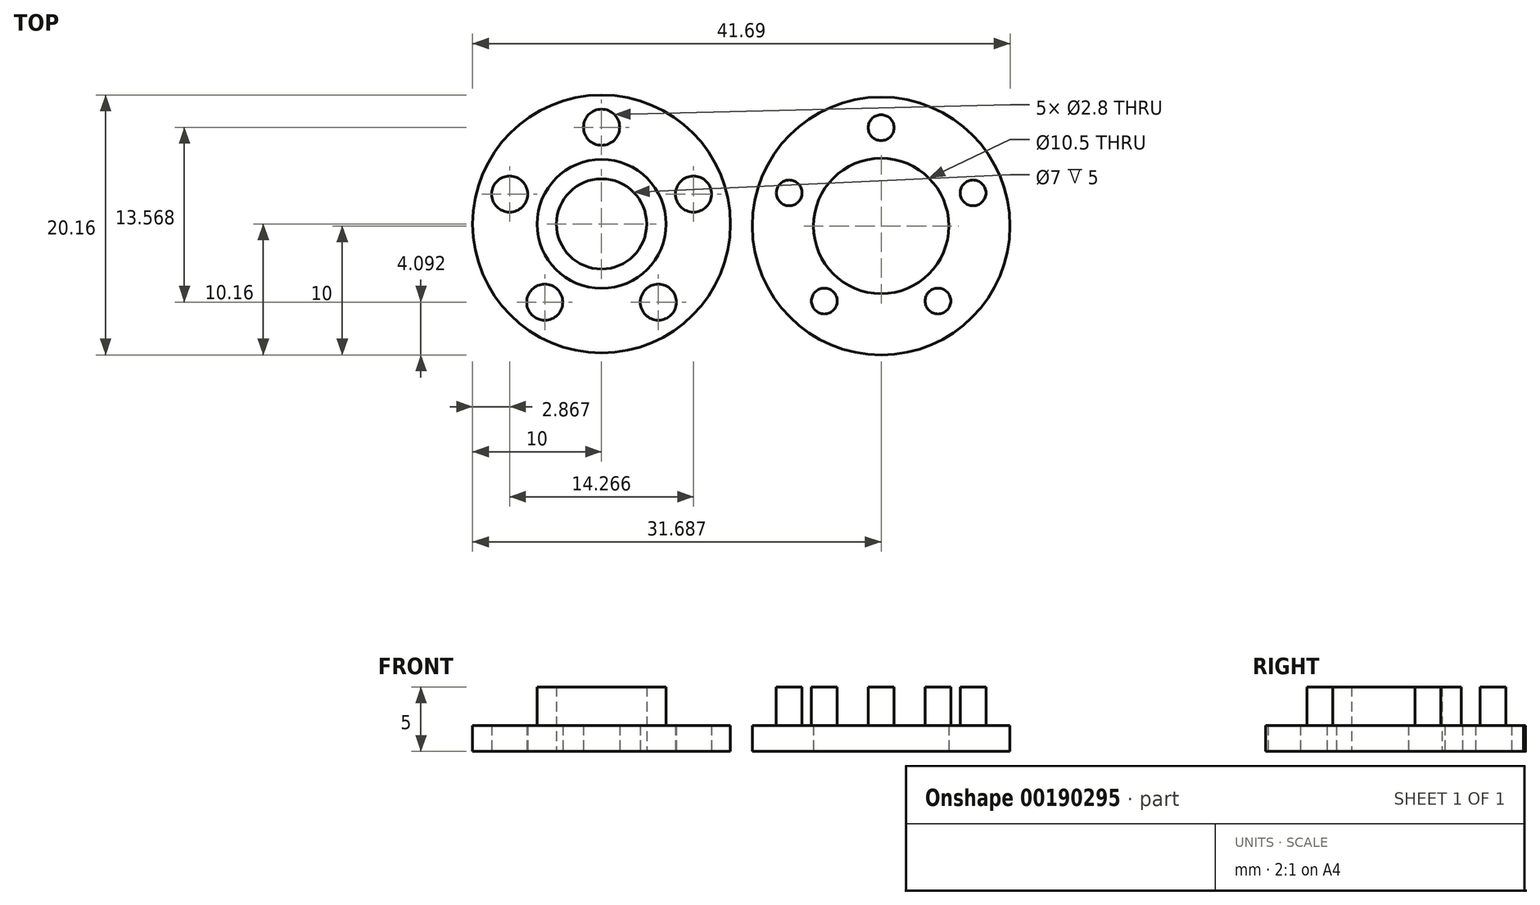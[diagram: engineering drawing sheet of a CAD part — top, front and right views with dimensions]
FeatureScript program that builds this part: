
annotation { "Feature Type Name" : "Feature", "Feature Type Description" : "" }
export const myFeature = defineFeature(function(context is Context, id is Id, definition is map)
    precondition{}
    {
        {
            var Q0;
            Q0=qCreatedBy(makeId("Top.planeOp"),FACE);
            var sketch = newSketch(context, id + "F0", { "sketchPlane" : qUnion([Q0])});
            skCircle(sketch, "E0", {"center": v(0, 0) * mm, "radius": 10 * mm});
            skCircle(sketch, "E1", {"center": v(0, 0) * mm, "radius": 5 * mm});
            skCircle(sketch, "E2", {"center": v(0, 7.5) * mm, "radius": 1.4 * mm});
            skLineSegment(sketch, "E3", {"start": v(0, 10) * mm, "end": v(0, 7.5) * mm, "construction": true});
            skLineSegment(sketch, "E4", {"start": v(0, 5) * mm, "end": v(0, 7.5) * mm, "construction": true});
            skCircle(sketch, "E5.1.0", {"center": v(-7.13, 2.32) * mm, "radius": 1.4 * mm});
            skCircle(sketch, "E5.2.0", {"center": v(-4.4, -6.07) * mm, "radius": 1.4 * mm});
            skCircle(sketch, "E5.3.0", {"center": v(4.4, -6.07) * mm, "radius": 1.4 * mm});
            skCircle(sketch, "E5.4.0", {"center": v(7.13, 2.32) * mm, "radius": 1.4 * mm});
            skSolve(sketch);
        }
        {
            var Q0;
            Q0=makeQuery(id+"F0.imprint","IMPRINT",FACE,{"disambiguationData":[TD([[makeQuery(id+"F0.imprint","IMPRINT",EDGE,{"derivedFrom":sQuery(id+"F0.wireOp",EDGE,"E0")}),1.0]])]});
            extrude(context, id + "F1", {"entities" : qUnion([Q0]), "depth" : 2 * mm});
        }
        {
            var Q0;
            Q0=qCreatedBy(makeId("Top.planeOp"),FACE);
            var sketch = newSketch(context, id + "F2", { "sketchPlane" : qUnion([Q0])});
            skCircle(sketch, "E6", {"center": v(21.69, -0.16) * mm, "radius": 10 * mm});
            skCircle(sketch, "E7", {"center": v(21.69, -0.16) * mm, "radius": 5.25 * mm});
            skCircle(sketch, "E8", {"center": v(21.69, 7.46) * mm, "radius": 1 * mm});
            skLineSegment(sketch, "E9", {"start": v(21.69, 9.84) * mm, "end": v(21.69, 7.46) * mm, "construction": true});
            skLineSegment(sketch, "E10", {"start": v(21.69, 5.09) * mm, "end": v(21.69, 7.46) * mm, "construction": true});
            skCircle(sketch, "E11.1.0", {"center": v(14.55, 2.4) * mm, "radius": 1 * mm});
            skCircle(sketch, "E11.2.0", {"center": v(17.28, -5.98) * mm, "radius": 1 * mm});
            skCircle(sketch, "E11.3.0", {"center": v(26.1, -5.98) * mm, "radius": 1 * mm});
            skCircle(sketch, "E11.4.0", {"center": v(28.82, 2.4) * mm, "radius": 1 * mm});
            skLineSegment(sketch, "E12", {"start": v(12.74, -4.62) * mm, "end": v(21.69, -0.16) * mm, "construction": true});
            skLineSegment(sketch, "E13", {"start": v(21.69, -0.16) * mm, "end": v(30.64, 4.3) * mm, "construction": true});
            skSolve(sketch);
        }
        {
            var Q0;
            Q0=qCreatedBy(makeId("Top.planeOp"),FACE);
            var sketch = newSketch(context, id + "F3", { "sketchPlane" : qUnion([Q0])});
            skCircle(sketch, "E14", {"center": v(0, 0) * mm, "radius": 3.5 * mm});
            skCircle(sketch, "E15", {"center": v(0, 0) * mm, "radius": 5 * mm});
            skSolve(sketch);
        }
        {
            var Q0;
            Q0=makeQuery(id+"F3.imprint","IMPRINT",FACE,{"disambiguationData":[TD([[makeQuery(id+"F3.imprint","IMPRINT",EDGE,{"derivedFrom":sQuery(id+"F3.wireOp",EDGE,"E14")}),-1.0]])]});
            extrude(context, id + "F4", {"entities" : qUnion([Q0]), "operationType" : NewBodyOperationType.ADD, "depth" : 5 * mm});
        }
        {
            var Q0;
            Q0=makeQuery(id+"F2.imprint","IMPRINT",FACE,{"disambiguationData":[TD([[makeQuery(id+"F2.imprint","IMPRINT",EDGE,{"derivedFrom":sQuery(id+"F2.wireOp",EDGE,"E6")}),1.0]])]});
            var Q1;
            Q1=makeQuery(id+"F2.imprint","IMPRINT",FACE,{"disambiguationData":[TD([[makeQuery(id+"F2.imprint","IMPRINT",EDGE,{"derivedFrom":sQuery(id+"F2.wireOp",EDGE,"E11.1.0")}),1.0]])]});
            var Q2;
            Q2=makeQuery(id+"F2.imprint","IMPRINT",FACE,{"disambiguationData":[TD([[makeQuery(id+"F2.imprint","IMPRINT",EDGE,{"derivedFrom":sQuery(id+"F2.wireOp",EDGE,"E8")}),1.0]])]});
            var Q3;
            Q3=makeQuery(id+"F2.imprint","IMPRINT",FACE,{"disambiguationData":[TD([[makeQuery(id+"F2.imprint","IMPRINT",EDGE,{"derivedFrom":sQuery(id+"F2.wireOp",EDGE,"E11.4.0")}),1.0]])]});
            var Q4;
            Q4=makeQuery(id+"F2.imprint","IMPRINT",FACE,{"disambiguationData":[TD([[makeQuery(id+"F2.imprint","IMPRINT",EDGE,{"derivedFrom":sQuery(id+"F2.wireOp",EDGE,"E11.3.0")}),1.0]])]});
            var Q5;
            Q5=makeQuery(id+"F2.imprint","IMPRINT",FACE,{"disambiguationData":[TD([[makeQuery(id+"F2.imprint","IMPRINT",EDGE,{"derivedFrom":sQuery(id+"F2.wireOp",EDGE,"E11.2.0")}),1.0]])]});
            extrude(context, id + "F5", {"entities" : qUnion([Q0, Q1, Q2, Q3, Q4, Q5]), "depth" : 2 * mm});
        }
        {
            var Q0;
            Q0=makeQuery(id+"F2.imprint","IMPRINT",FACE,{"disambiguationData":[TD([[makeQuery(id+"F2.imprint","IMPRINT",EDGE,{"derivedFrom":sQuery(id+"F2.wireOp",EDGE,"E8")}),1.0]])]});
            var Q1;
            Q1=makeQuery(id+"F2.imprint","IMPRINT",FACE,{"disambiguationData":[TD([[makeQuery(id+"F2.imprint","IMPRINT",EDGE,{"derivedFrom":sQuery(id+"F2.wireOp",EDGE,"E11.4.0")}),1.0]])]});
            var Q2;
            Q2=makeQuery(id+"F2.imprint","IMPRINT",FACE,{"disambiguationData":[TD([[makeQuery(id+"F2.imprint","IMPRINT",EDGE,{"derivedFrom":sQuery(id+"F2.wireOp",EDGE,"E11.3.0")}),1.0]])]});
            var Q3;
            Q3=makeQuery(id+"F2.imprint","IMPRINT",FACE,{"disambiguationData":[TD([[makeQuery(id+"F2.imprint","IMPRINT",EDGE,{"derivedFrom":sQuery(id+"F2.wireOp",EDGE,"E11.2.0")}),1.0]])]});
            var Q4;
            Q4=makeQuery(id+"F2.imprint","IMPRINT",FACE,{"disambiguationData":[TD([[makeQuery(id+"F2.imprint","IMPRINT",EDGE,{"derivedFrom":sQuery(id+"F2.wireOp",EDGE,"E11.1.0")}),1.0]])]});
            extrude(context, id + "F6", {"entities" : qUnion([Q0, Q1, Q2, Q3, Q4]), "operationType" : NewBodyOperationType.ADD, "depth" : 5 * mm});
        }
    });
